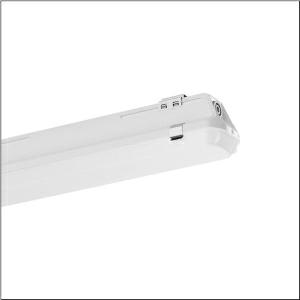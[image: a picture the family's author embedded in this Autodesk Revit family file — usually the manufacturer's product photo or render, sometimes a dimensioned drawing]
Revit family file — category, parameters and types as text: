
# Revit family: monsun_r__11_51fp108p430h_5d5d
name_source: partatom
category: Lighting Fixtures
units: mm (PartAtom-declared; Revit-internal decimal feet)

## family parameters
Cut with Voids When Loaded = No
Host = Face
Light Source = No
Part Type = Normal
Room Calculation Point = No
Round Connector Dimension = Use Diameter
Shared = No

## types (1)
- Monsun® 11 (1 x LED, 3970 lm, 22.2 W, 4000K)
    Apparent Load = 22 VA
    CIE Flux Codes = 47 77 93 94 100
    Color Rendering = 80
    Color Temperature = 4000K
    Default Elevation = 1800 mm
    Description = Monsun® 11, damp-proof luminaire, chain hanger, primary optical cover: enclosure, of PMMA, light emission: direct distribution, primary light characteristic: symmetric, installation type: suspended mounting, surface-mounted, horizontal mounting, vertical mounting, LED, rated luminous flux: 3.970lm, luminous efficacy: 179lm/W, light colour: 840, colour temperature: 4000K, control gear: ECG, with terminal, 3-pole, max. 2.5mm², mains connection: 220..240V, AC, 50/60Hz, rated input power: 22W, luminaire housing, of glass-fibre reinforced polyester, uncoated, bright grey, incl. chain hanger, length: 1.590mm, width: 90mm, height: 88mm, clip for enclosure, of stainless steel (V2A), ceiling mounting element, of stainless steel (V2A), chain hanger, of stainless steel (V2A), protection rating (complete): IP66, insulation class (complete): insulation class I (protective earthing), certification: CE, ENEC, VDE, UKCA, protection symbol: D, impact resistance: IK04, permissible operating ambient temperature: -35..+40°C, standard: EN 50419, EN 60598-2-1, no direct snow, no direct sun, no direct rain, for indoor or canopied outdoor use, corresponds to IFS (International Featured Standards) requirements for safety and quality in the food industry, contact your sales advisor before using the luminaires in applications with unclear chemical exposure, large temperature fluctuations or condensation-forming humidity, LABS conformity tested according to VDMA 24364:2018-05, packaging unit: 1 piece
    Height = 89 mm
    Lamp = 1 x LED
    Lamp Light Flux = 3970 lm
    Lamp Power = 22.2 W
    Lamp count = 1
    Length = 1590 mm
    Luminous efficacy = 179 lm/W
    Manufacturer = Siteco
    ModVariant = No
    Model = 51FP108P430H
    Mounting Place = Ceiling
    Mounting Type = Surface mounted
    Number of Poles = 1
    OnlyDefault = Yes
    Power Factor = 1
    Product Name = Monsun® 11
    Product group = damp-proof luminaire
    ProductGroupID = 300
    Protection Class = Protection class I
    Protection Degree = IP 66
    RLX_Detail_Level = 1
    RLX_Emergency_Light_Flux = 0 lm
    RLX_Emergency_Type = 0
    RLX_Emergency_Type_DB = No
    RlxData = <blob elided: 88453 chars, md5=02053333>
    Socket = socket
    Standby Power = 0 W
    System Light Flux = 3970 lm
    System Power = 22 W
    Type Comments = Product without accessories
    Type Image = l_1319650.jpg
    URL = http://relux.com
    VarID = ---
    Voltage = 0 V
    Weight = 0.00 kg
    Width = 90 mm

## geometry (parser evidence)
native form markers: Blend x4, Sweep x13
no freeform markers — native parametric forms only
